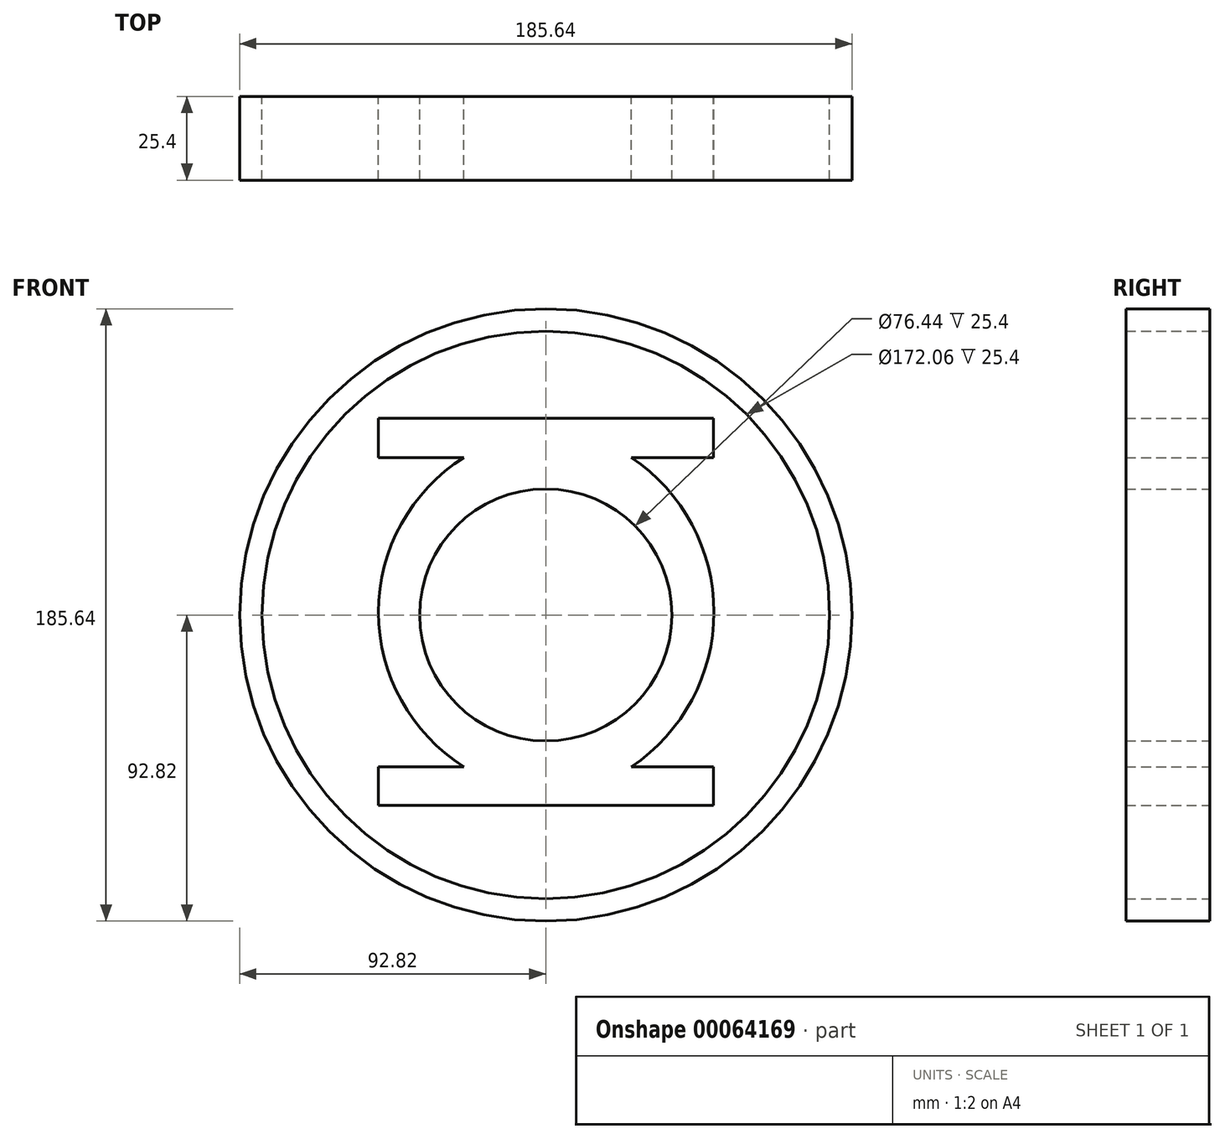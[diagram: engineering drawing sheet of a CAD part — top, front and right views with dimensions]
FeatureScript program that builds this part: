
annotation { "Feature Type Name" : "Feature", "Feature Type Description" : "" }
export const myFeature = defineFeature(function(context is Context, id is Id, definition is map)
    precondition{}
    {
        {
            var Q0;
            Q0=qCreatedBy(makeId("Front.planeOp"),FACE);
            var sketch = newSketch(context, id + "F0", { "sketchPlane" : qUnion([Q0])});
            skLineSegment(sketch, "E0", {"start": v(-50.8, 59.66) * mm, "end": v(-50.8, 47.72) * mm});
            skLineSegment(sketch, "E1", {"start": v(-50.8, 47.72) * mm, "end": v(-24.85, 47.72) * mm});
            skLineSegment(sketch, "E2", {"start": v(-50.8, 59.66) * mm, "end": v(50.8, 59.66) * mm});
            skLineSegment(sketch, "E3", {"start": v(50.8, 59.66) * mm, "end": v(50.8, 47.72) * mm});
            skLineSegment(sketch, "E4", {"start": v(50.8, 47.72) * mm, "end": v(25.95, 47.72) * mm});
            skLineSegment(sketch, "E5", {"start": v(-24.85, -46) * mm, "end": v(-50.8, -46) * mm});
            skLineSegment(sketch, "E6", {"start": v(-50.8, -46) * mm, "end": v(-50.8, -57.69) * mm});
            skLineSegment(sketch, "E7", {"start": v(-50.8, -57.69) * mm, "end": v(50.8, -57.69) * mm});
            skLineSegment(sketch, "E8", {"start": v(50.8, -57.69) * mm, "end": v(50.8, -46) * mm});
            skLineSegment(sketch, "E9", {"start": v(50.8, -46) * mm, "end": v(25.95, -46) * mm});
            skArc(sketch, "E10", {"start": v(-24.85, 47.72) * mm, "mid": v(-50.72, 0.86) * mm, "end": v(-24.85, -46) * mm});
            skArc(sketch, "E11", {"start": v(25.95, -46) * mm, "mid": v(50.98, 0.86) * mm, "end": v(25.95, 47.72) * mm});
            skCircle(sketch, "E12", {"center": v(0, 0) * mm, "radius": 38.22 * mm});
            skCircle(sketch, "E13", {"center": v(0, 0) * mm, "radius": 86.03 * mm});
            skCircle(sketch, "E14", {"center": v(0, 0) * mm, "radius": 92.82 * mm});
            skSolve(sketch);
        }
        {
            var Q0;
            Q0=makeQuery(id+"F0.imprint","IMPRINT",FACE,{"disambiguationData":[TD([[makeQuery(id+"F0.imprint","IMPRINT",EDGE,{"derivedFrom":sQuery(id+"F0.wireOp",EDGE,"E13")}),-1.0]])]});
            var Q1;
            Q1=makeQuery(id+"F0.imprint","IMPRINT",FACE,{"disambiguationData":[TD([[makeQuery(id+"F0.imprint","IMPRINT",EDGE,{"derivedFrom":sQuery(id+"F0.wireOp",EDGE,"E0")}),1.0]])]});
            extrude(context, id + "F1", {"entities" : qUnion([Q0, Q1]), "depth" : 25.4 * mm});
        }
    });
